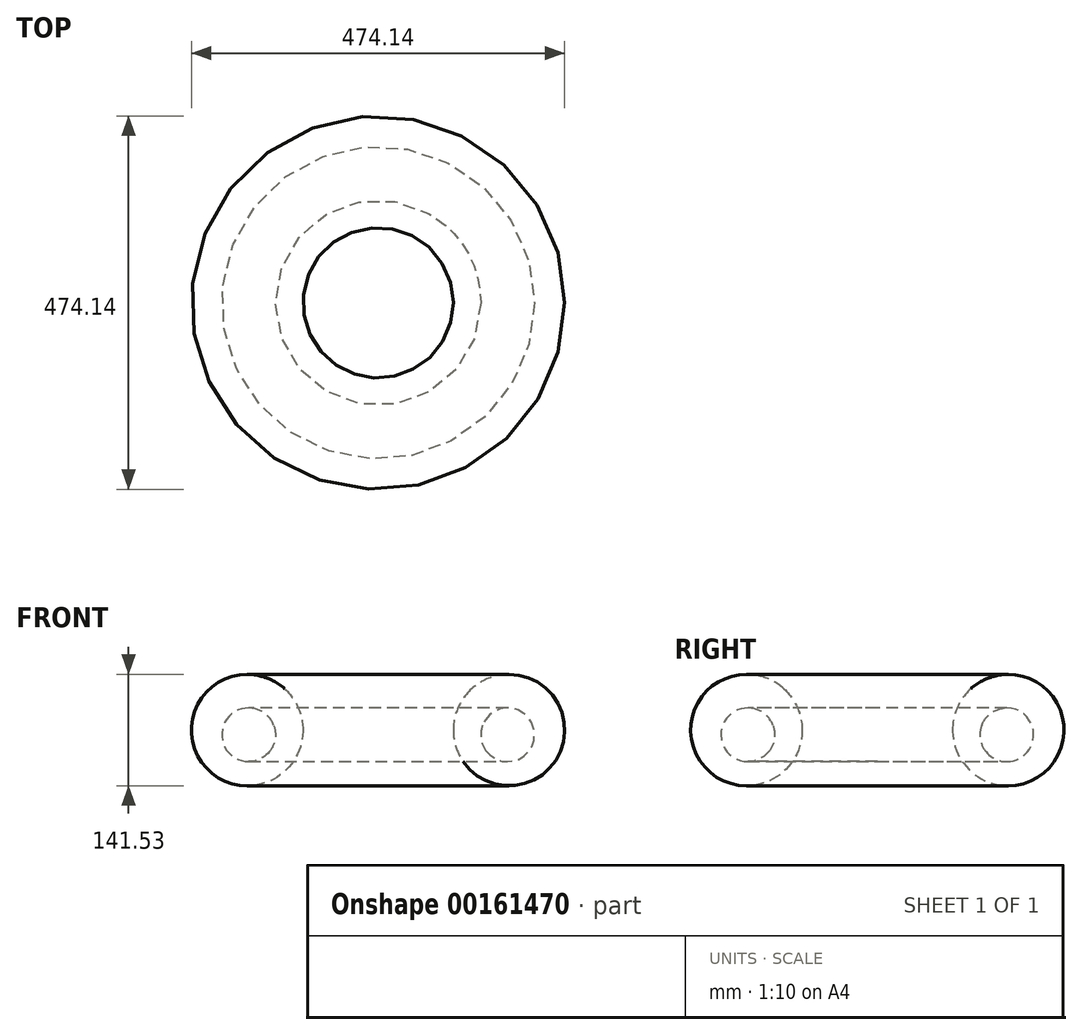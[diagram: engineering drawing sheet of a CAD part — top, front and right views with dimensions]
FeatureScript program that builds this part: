
annotation { "Feature Type Name" : "Feature", "Feature Type Description" : "" }
export const myFeature = defineFeature(function(context is Context, id is Id, definition is map)
    precondition{}
    {
        {
            var Q0;
            Q0=qCreatedBy(makeId("Front.planeOp"),FACE);
            var sketch = newSketch(context, id + "F0", { "sketchPlane" : qUnion([Q0])});
            skArc(sketch, "E0", {"start": v(28.12, 17.4) * mm, "mid": v(-37.55, 9.5) * mm, "end": v(24.08, -14.5) * mm});
            skArc(sketch, "E1", {"start": v(24.08, -14.5) * mm, "mid": v(30.06, 0.95) * mm, "end": v(28.12, 17.4) * mm});
            skArc(sketch, "E2", {"start": v(42.04, 63.58) * mm, "mid": v(-69.6, -18.9) * mm, "end": v(65.14, 14.46) * mm});
            skArc(sketch, "E3", {"start": v(65.14, 14.46) * mm, "mid": v(58.49, 41.32) * mm, "end": v(42.04, 63.58) * mm});
            skLineSegment(sketch, "E4", {"start": v(160.75, 32.68) * mm, "end": v(160.75, -27.36) * mm, "construction": true});
            skSolve(sketch);
        }
        {
            var Q0;
            Q0 = qSketchRegion(id + "F0", true);
            var Q1;
            Q1=sQuery(id+"F0.wireOp",EDGE,"E4");
            revolve(context, id + "F1", {"entities" : qUnion([Q0]), "axis" : qUnion([Q1]), "revolveType" : RevolveType.FULL});
        }
    });
